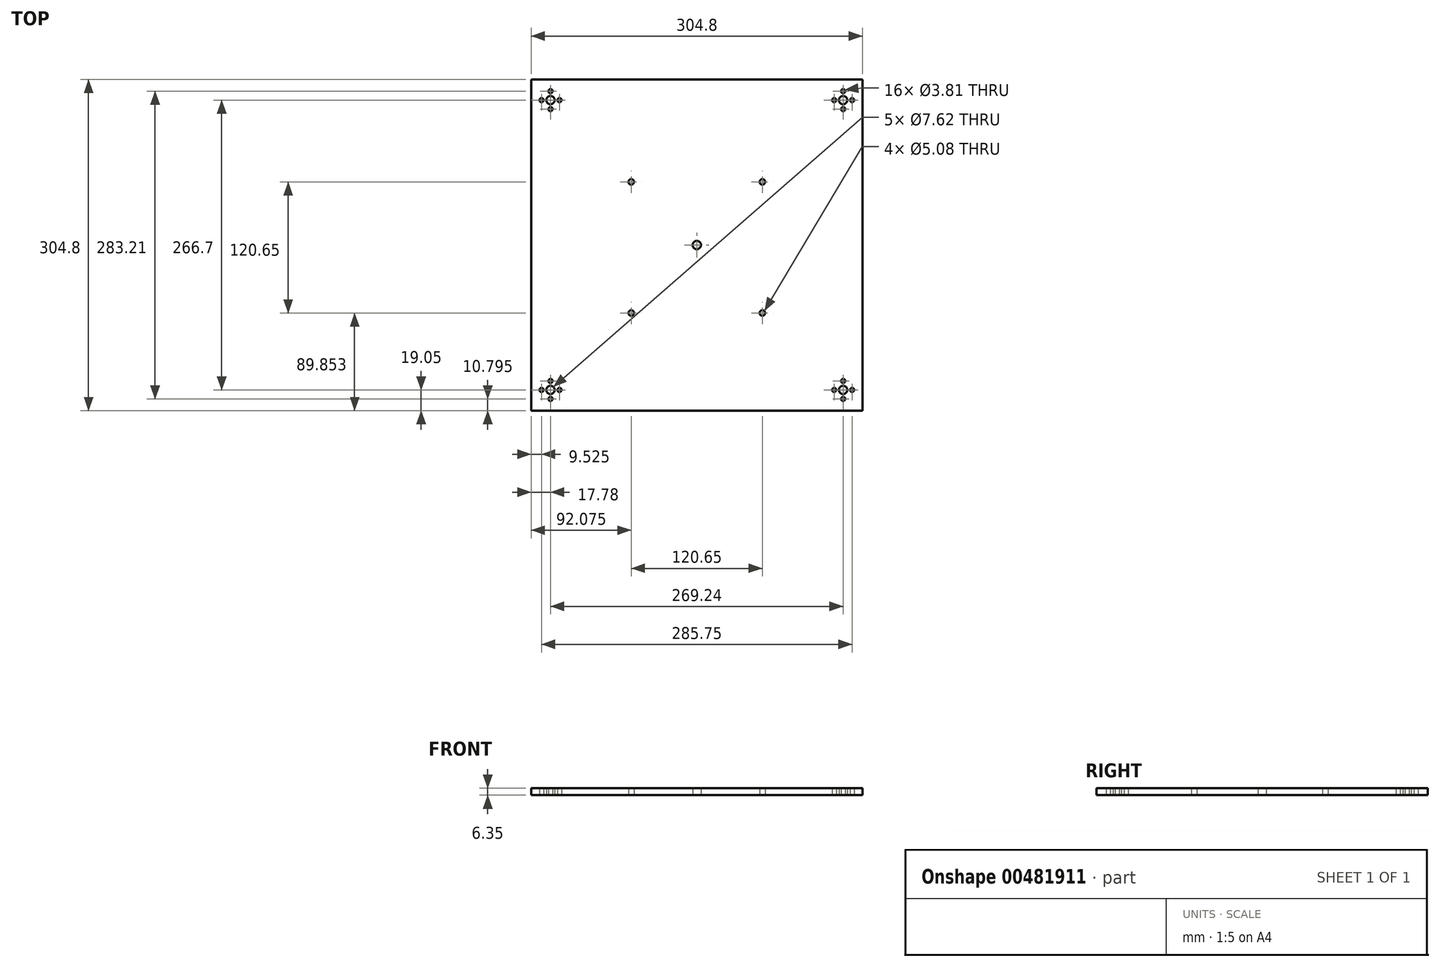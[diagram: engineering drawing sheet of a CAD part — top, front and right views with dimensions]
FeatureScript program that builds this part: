
annotation { "Feature Type Name" : "Feature", "Feature Type Description" : "" }
export const myFeature = defineFeature(function(context is Context, id is Id, definition is map)
    precondition{}
    {
        {
            var Q0;
            Q0=qCreatedBy(makeId("Top.planeOp"),FACE);
            var sketch = newSketch(context, id + "F0", { "sketchPlane" : qUnion([Q0])});
            skLineSegment(sketch, "E0.bottom", {"start": v(0, 0) * mm, "end": v(304.8, 0) * mm});
            skLineSegment(sketch, "E0.top", {"start": v(0, -304.8) * mm, "end": v(304.8, -304.8) * mm});
            skLineSegment(sketch, "E0.left", {"start": v(0, 0) * mm, "end": v(0, -304.8) * mm});
            skLineSegment(sketch, "E0.right", {"start": v(304.8, 0) * mm, "end": v(304.8, -304.8) * mm});
            skCircle(sketch, "E1", {"center": v(152.4, -152.4) * mm, "radius": 3.81 * mm});
            skCircle(sketch, "E2", {"center": v(59.69, -19.05) * mm, "radius": 3.81 * mm});
            skCircle(sketch, "E3", {"center": v(245.1, -19.05) * mm, "radius": 3.81 * mm});
            skCircle(sketch, "E4", {"center": v(59.7, -285.75) * mm, "radius": 3.81 * mm});
            skCircle(sketch, "E5", {"center": v(245.11, -285.75) * mm, "radius": 3.81 * mm});
            skCircle(sketch, "E6", {"center": v(59.7, -277.5) * mm, "radius": 1.9 * mm});
            skCircle(sketch, "E7", {"center": v(67.95, -285.75) * mm, "radius": 1.9 * mm});
            skCircle(sketch, "E8", {"center": v(59.7, -294) * mm, "radius": 1.9 * mm});
            skCircle(sketch, "E9", {"center": v(51.44, -285.75) * mm, "radius": 1.9 * mm});
            skCircle(sketch, "E10", {"center": v(245.11, -277.5) * mm, "radius": 1.9 * mm});
            skCircle(sketch, "E11", {"center": v(236.85, -285.75) * mm, "radius": 1.9 * mm});
            skCircle(sketch, "E12", {"center": v(245.1, -294) * mm, "radius": 1.9 * mm});
            skCircle(sketch, "E13", {"center": v(253.37, -285.75) * mm, "radius": 1.9 * mm});
            skCircle(sketch, "E14", {"center": v(245.1, -27.3) * mm, "radius": 1.9 * mm});
            skCircle(sketch, "E15", {"center": v(245.1, -10.8) * mm, "radius": 1.9 * mm});
            skCircle(sketch, "E16", {"center": v(253.37, -19.05) * mm, "radius": 1.9 * mm});
            skCircle(sketch, "E17", {"center": v(236.85, -19.05) * mm, "radius": 1.9 * mm});
            skCircle(sketch, "E18", {"center": v(59.7, -10.8) * mm, "radius": 1.9 * mm});
            skCircle(sketch, "E19", {"center": v(59.7, -27.3) * mm, "radius": 1.9 * mm});
            skCircle(sketch, "E20", {"center": v(67.95, -19.05) * mm, "radius": 1.9 * mm});
            skCircle(sketch, "E21", {"center": v(51.43, -19.05) * mm, "radius": 1.9 * mm});
            skCircle(sketch, "E22", {"center": v(92.07, -94.3) * mm, "radius": 2.54 * mm});
            skCircle(sketch, "E23", {"center": v(212.72, -94.3) * mm, "radius": 2.54 * mm});
            skCircle(sketch, "E24", {"center": v(92.07, -214.95) * mm, "radius": 2.54 * mm});
            skCircle(sketch, "E25", {"center": v(212.72, -214.95) * mm, "radius": 2.54 * mm});
            skLineSegment(sketch, "E26", {"start": v(41.91, 0) * mm, "end": v(41.91, -66.27) * mm});
            skLineSegment(sketch, "E27", {"start": v(35.56, 0) * mm, "end": v(35.56, -65.6) * mm});
            skLineSegment(sketch, "E28", {"start": v(38.73, 0) * mm, "end": v(38.73, -13.4) * mm});
            skCircle(sketch, "E29.MirrorC", {"center": v(17.78, -19.05) * mm, "radius": 3.81 * mm});
            skCircle(sketch, "E30.MirrorC", {"center": v(17.78, -10.8) * mm, "radius": 1.9 * mm});
            skCircle(sketch, "E31.MirrorC", {"center": v(26.03, -19.05) * mm, "radius": 1.9 * mm});
            skCircle(sketch, "E32.MirrorC", {"center": v(17.78, -27.3) * mm, "radius": 1.9 * mm});
            skCircle(sketch, "E33.MirrorC", {"center": v(9.52, -19.05) * mm, "radius": 1.9 * mm});
            skLineSegment(sketch, "E34", {"start": v(152.4, 0) * mm, "end": v(152.4, -304.8) * mm});
            skLineSegment(sketch, "E35", {"start": v(0, -152.4) * mm, "end": v(304.8, -152.4) * mm});
            skCircle(sketch, "E36.MirrorC", {"center": v(287.02, -10.8) * mm, "radius": 1.9 * mm});
            skCircle(sketch, "E37.MirrorC", {"center": v(287.02, -19.05) * mm, "radius": 3.81 * mm});
            skCircle(sketch, "E38.MirrorC", {"center": v(295.27, -19.05) * mm, "radius": 1.9 * mm});
            skCircle(sketch, "E39.MirrorC", {"center": v(278.76, -19.05) * mm, "radius": 1.9 * mm});
            skCircle(sketch, "E40.MirrorC", {"center": v(287.02, -27.3) * mm, "radius": 1.9 * mm});
            skCircle(sketch, "E41.MirrorC", {"center": v(17.78, -277.5) * mm, "radius": 1.9 * mm});
            skCircle(sketch, "E42.MirrorC", {"center": v(17.78, -285.75) * mm, "radius": 3.81 * mm});
            skCircle(sketch, "E43.MirrorC", {"center": v(9.52, -285.75) * mm, "radius": 1.9 * mm});
            skCircle(sketch, "E44.MirrorC", {"center": v(26.03, -285.75) * mm, "radius": 1.9 * mm});
            skCircle(sketch, "E45.MirrorC", {"center": v(17.78, -294) * mm, "radius": 1.9 * mm});
            skCircle(sketch, "E46.MirrorC", {"center": v(287.02, -285.75) * mm, "radius": 3.81 * mm});
            skCircle(sketch, "E47.MirrorC", {"center": v(287.02, -294) * mm, "radius": 1.9 * mm});
            skCircle(sketch, "E48.MirrorC", {"center": v(295.27, -285.75) * mm, "radius": 1.9 * mm});
            skCircle(sketch, "E49.MirrorC", {"center": v(287.02, -277.5) * mm, "radius": 1.9 * mm});
            skCircle(sketch, "E50.MirrorC", {"center": v(278.76, -285.75) * mm, "radius": 1.9 * mm});
            skSolve(sketch);
        }
        {
            var Q0;
            Q0=makeQuery(id+"F0.imprint","IMPRINT",FACE,{"disambiguationData":[TD([[makeQuery(id+"F0.imprint","IMPRINT",EDGE,{"derivedFrom":sQuery(id+"F0.wireOp",EDGE,"E0.bottom")}),-1.0]])]});
            var Q1;
            Q1=makeQuery(id+"F0.imprint","IMPRINT",FACE,{"disambiguationData":[TD([[makeQuery(id+"F0.imprint","IMPRINT",EDGE,{"derivedFrom":sQuery(id+"F0.wireOp",EDGE,"E3")}),-1.0]])]});
            var Q2;
            Q2=makeQuery(id+"F0.imprint","IMPRINT",FACE,{"disambiguationData":[TD([[makeQuery(id+"F0.imprint","IMPRINT",EDGE,{"derivedFrom":sQuery(id+"F0.wireOp",EDGE,"E4")}),-1.0]])]});
            var Q3;
            Q3=makeQuery(id+"F0.imprint","IMPRINT",FACE,{"disambiguationData":[TD([[makeQuery(id+"F0.imprint","IMPRINT",EDGE,{"derivedFrom":sQuery(id+"F0.wireOp",EDGE,"E4")}),1.0]])]});
            var Q4;
            Q4=makeQuery(id+"F0.imprint","IMPRINT",FACE,{"disambiguationData":[TD([[makeQuery(id+"F0.imprint","IMPRINT",EDGE,{"derivedFrom":sQuery(id+"F0.wireOp",EDGE,"E8")}),1.0]])]});
            var Q5;
            Q5=makeQuery(id+"F0.imprint","IMPRINT",FACE,{"disambiguationData":[TD([[makeQuery(id+"F0.imprint","IMPRINT",EDGE,{"derivedFrom":sQuery(id+"F0.wireOp",EDGE,"E7")}),1.0]])]});
            var Q6;
            Q6=makeQuery(id+"F0.imprint","IMPRINT",FACE,{"disambiguationData":[TD([[makeQuery(id+"F0.imprint","IMPRINT",EDGE,{"derivedFrom":sQuery(id+"F0.wireOp",EDGE,"E6")}),1.0]])]});
            var Q7;
            Q7=makeQuery(id+"F0.imprint","IMPRINT",FACE,{"disambiguationData":[TD([[makeQuery(id+"F0.imprint","IMPRINT",EDGE,{"derivedFrom":sQuery(id+"F0.wireOp",EDGE,"E9")}),1.0]])]});
            var Q8;
            Q8=makeQuery(id+"F0.imprint","IMPRINT",FACE,{"disambiguationData":[TD([[makeQuery(id+"F0.imprint","IMPRINT",EDGE,{"derivedFrom":sQuery(id+"F0.wireOp",EDGE,"E5")}),1.0]])]});
            var Q9;
            Q9=makeQuery(id+"F0.imprint","IMPRINT",FACE,{"disambiguationData":[TD([[makeQuery(id+"F0.imprint","IMPRINT",EDGE,{"derivedFrom":sQuery(id+"F0.wireOp",EDGE,"E5")}),-1.0]])]});
            var Q10;
            Q10=makeQuery(id+"F0.imprint","IMPRINT",FACE,{"disambiguationData":[TD([[makeQuery(id+"F0.imprint","IMPRINT",EDGE,{"derivedFrom":sQuery(id+"F0.wireOp",EDGE,"E10")}),1.0]])]});
            var Q11;
            Q11=makeQuery(id+"F0.imprint","IMPRINT",FACE,{"disambiguationData":[TD([[makeQuery(id+"F0.imprint","IMPRINT",EDGE,{"derivedFrom":sQuery(id+"F0.wireOp",EDGE,"E11")}),1.0]])]});
            var Q12;
            Q12=makeQuery(id+"F0.imprint","IMPRINT",FACE,{"disambiguationData":[TD([[makeQuery(id+"F0.imprint","IMPRINT",EDGE,{"derivedFrom":sQuery(id+"F0.wireOp",EDGE,"E12")}),1.0]])]});
            var Q13;
            Q13=makeQuery(id+"F0.imprint","IMPRINT",FACE,{"disambiguationData":[TD([[makeQuery(id+"F0.imprint","IMPRINT",EDGE,{"derivedFrom":sQuery(id+"F0.wireOp",EDGE,"E13")}),1.0]])]});
            var Q14;
            Q14=makeQuery(id+"F0.imprint","IMPRINT",FACE,{"disambiguationData":[TD([[makeQuery(id+"F0.imprint","IMPRINT",EDGE,{"derivedFrom":sQuery(id+"F0.wireOp",EDGE,"E3")}),1.0]])]});
            var Q15;
            Q15=makeQuery(id+"F0.imprint","IMPRINT",FACE,{"disambiguationData":[TD([[makeQuery(id+"F0.imprint","IMPRINT",EDGE,{"derivedFrom":sQuery(id+"F0.wireOp",EDGE,"E16")}),1.0]])]});
            var Q16;
            Q16=makeQuery(id+"F0.imprint","IMPRINT",FACE,{"disambiguationData":[TD([[makeQuery(id+"F0.imprint","IMPRINT",EDGE,{"derivedFrom":sQuery(id+"F0.wireOp",EDGE,"E15")}),1.0]])]});
            var Q17;
            Q17=makeQuery(id+"F0.imprint","IMPRINT",FACE,{"disambiguationData":[TD([[makeQuery(id+"F0.imprint","IMPRINT",EDGE,{"derivedFrom":sQuery(id+"F0.wireOp",EDGE,"E14")}),1.0]])]});
            var Q18;
            Q18=makeQuery(id+"F0.imprint","IMPRINT",FACE,{"disambiguationData":[TD([[makeQuery(id+"F0.imprint","IMPRINT",EDGE,{"derivedFrom":sQuery(id+"F0.wireOp",EDGE,"E17")}),1.0]])]});
            var Q19;
            Q19=makeQuery(id+"F0.imprint","IMPRINT",FACE,{"disambiguationData":[TD([[makeQuery(id+"F0.imprint","IMPRINT",EDGE,{"derivedFrom":sQuery(id+"F0.wireOp",EDGE,"E2")}),1.0]])]});
            var Q20;
            Q20=makeQuery(id+"F0.imprint","IMPRINT",FACE,{"disambiguationData":[TD([[makeQuery(id+"F0.imprint","IMPRINT",EDGE,{"derivedFrom":sQuery(id+"F0.wireOp",EDGE,"E18")}),1.0]])]});
            var Q21;
            Q21=makeQuery(id+"F0.imprint","IMPRINT",FACE,{"disambiguationData":[TD([[makeQuery(id+"F0.imprint","IMPRINT",EDGE,{"derivedFrom":sQuery(id+"F0.wireOp",EDGE,"E20")}),1.0]])]});
            var Q22;
            Q22=makeQuery(id+"F0.imprint","IMPRINT",FACE,{"disambiguationData":[TD([[makeQuery(id+"F0.imprint","IMPRINT",EDGE,{"derivedFrom":sQuery(id+"F0.wireOp",EDGE,"E19")}),1.0]])]});
            var Q23;
            Q23=makeQuery(id+"F0.imprint","IMPRINT",FACE,{"disambiguationData":[TD([[makeQuery(id+"F0.imprint","IMPRINT",EDGE,{"derivedFrom":sQuery(id+"F0.wireOp",EDGE,"E21")}),1.0]])]});
            extrude(context, id + "F1", {"entities" : qUnion([Q0, Q1, Q2, Q3, Q4, Q5, Q6, Q7, Q8, Q9, Q10, Q11, Q12, Q13, Q14, Q15, Q16, Q17, Q18, Q19, Q20, Q21, Q22, Q23]), "depth" : 6.35 * mm, "offsetDistance" : 25.4 * mm});
        }
    });
